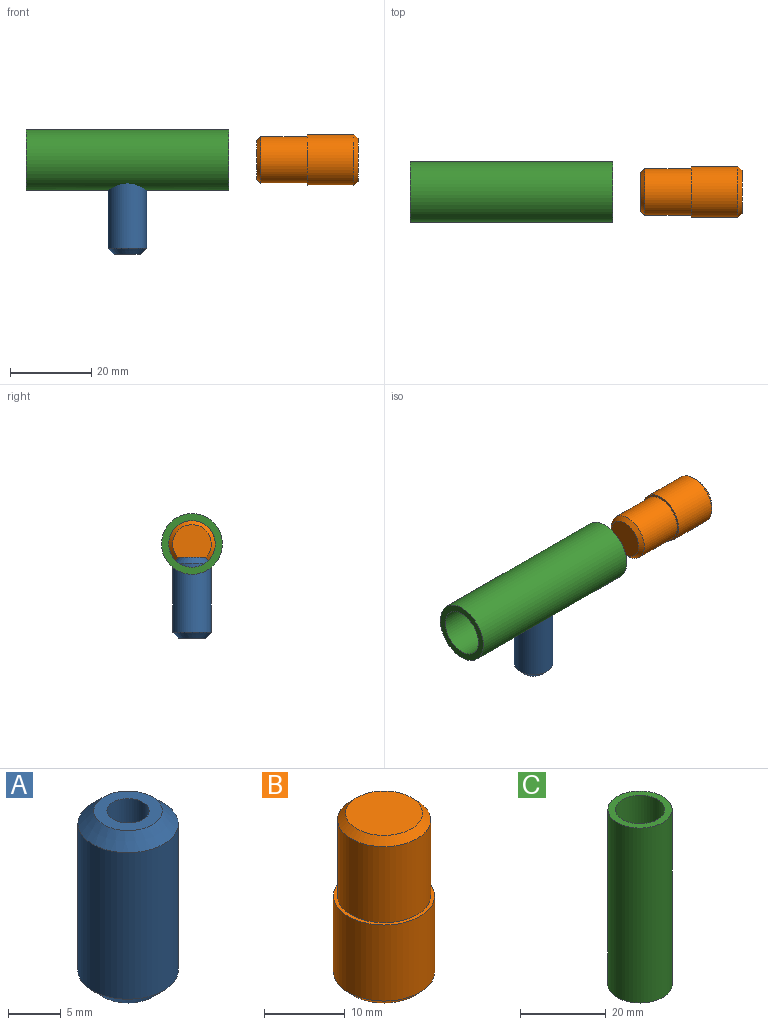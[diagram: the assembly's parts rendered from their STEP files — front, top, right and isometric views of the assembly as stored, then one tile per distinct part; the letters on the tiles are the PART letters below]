
ASSEMBLY  parts=3 mates=2
PART A: 6 faces, bbox 9.5x9.5x20 mm
  f0: cylinder r=4.75mm len=17mm, axis (0,0,-1), area 507.4mm2, adj f4,f5
  f1: plane 6.5x6.5mm, normal (0,0,1), area 20.6mm2, adj f3,f4
  f2: plane 6.5x6.5mm, normal (0,0,-1), area 20.6mm2, adj f3,f5
  f3: cylinder r=2mm len=20mm, axis (0,0,1), area 251.3mm2, adj f1,f2
  f4: cone r=3.25mm half-angle=45deg, axis (0,0,-1), area 53.3mm2, adj f0,f1
  f5: cone r=4.75mm half-angle=45deg, axis (0,0,1), area 53.3mm2, adj f0,f2
PART B: 7 faces, bbox 12.5x12.5x25 mm
  f0: cylinder r=5.75mm len=11.5mm, axis (0,0,-1), area 415.5mm2, adj f3,f6
  f1: plane 9.5x9.5mm, normal (0,0,1), area 70.9mm2, adj f6
  f2: cylinder r=6.25mm len=12.5mm, axis (0,0,-1), area 451.6mm2, adj f3,f5
  f3: plane 12.5x12.5mm, normal (0,0,1), area 18.8mm2, adj f0,f2
  f4: plane 10.5x10.5mm, normal (0,0,-1), area 86.6mm2, adj f5
  f5: cone r=6.25mm half-angle=45deg, axis (0,0,1), area 51.1mm2, adj f2,f4
  f6: cone r=4.75mm half-angle=45deg, axis (0,0,-1), area 46.7mm2, adj f0,f1
PART C: 5 faces, bbox 15x15x50 mm
  f0: cylinder r=5.75mm len=50mm, axis (0,0,-1), area 1752.3mm2, adj f2,f3,f4
  f1: cylinder r=7.5mm len=50mm, axis (0,0,-1), area 2303.8mm2, adj f2,f3,f4
  f2: plane 15x15mm, normal (0,0,1), area 72.8mm2, adj f0,f1
  f3: plane 15x15mm, normal (0,0,-1), area 72.8mm2, adj f0,f1
  f4: cylinder r=4mm len=8mm, axis (0,-1,0), area 49.3mm2, adj f0,f1
PLACE A t=(0,0,-17.5)mm
PLACE B rot(axis=(0,-1,0),90deg) t=(56.89,0,-26.19)mm
PLACE C rot(axis=(-0.58,0.58,-0.58),120deg) t=(-25,-30,5.81)mm
MATE slider C.f0 <-> B.f0  axis (1,0,0) through (25,0,5.81)mm
MATE slider C.f4 <-> A.f0  axis (0,0,1) through (0,0,0)mm
